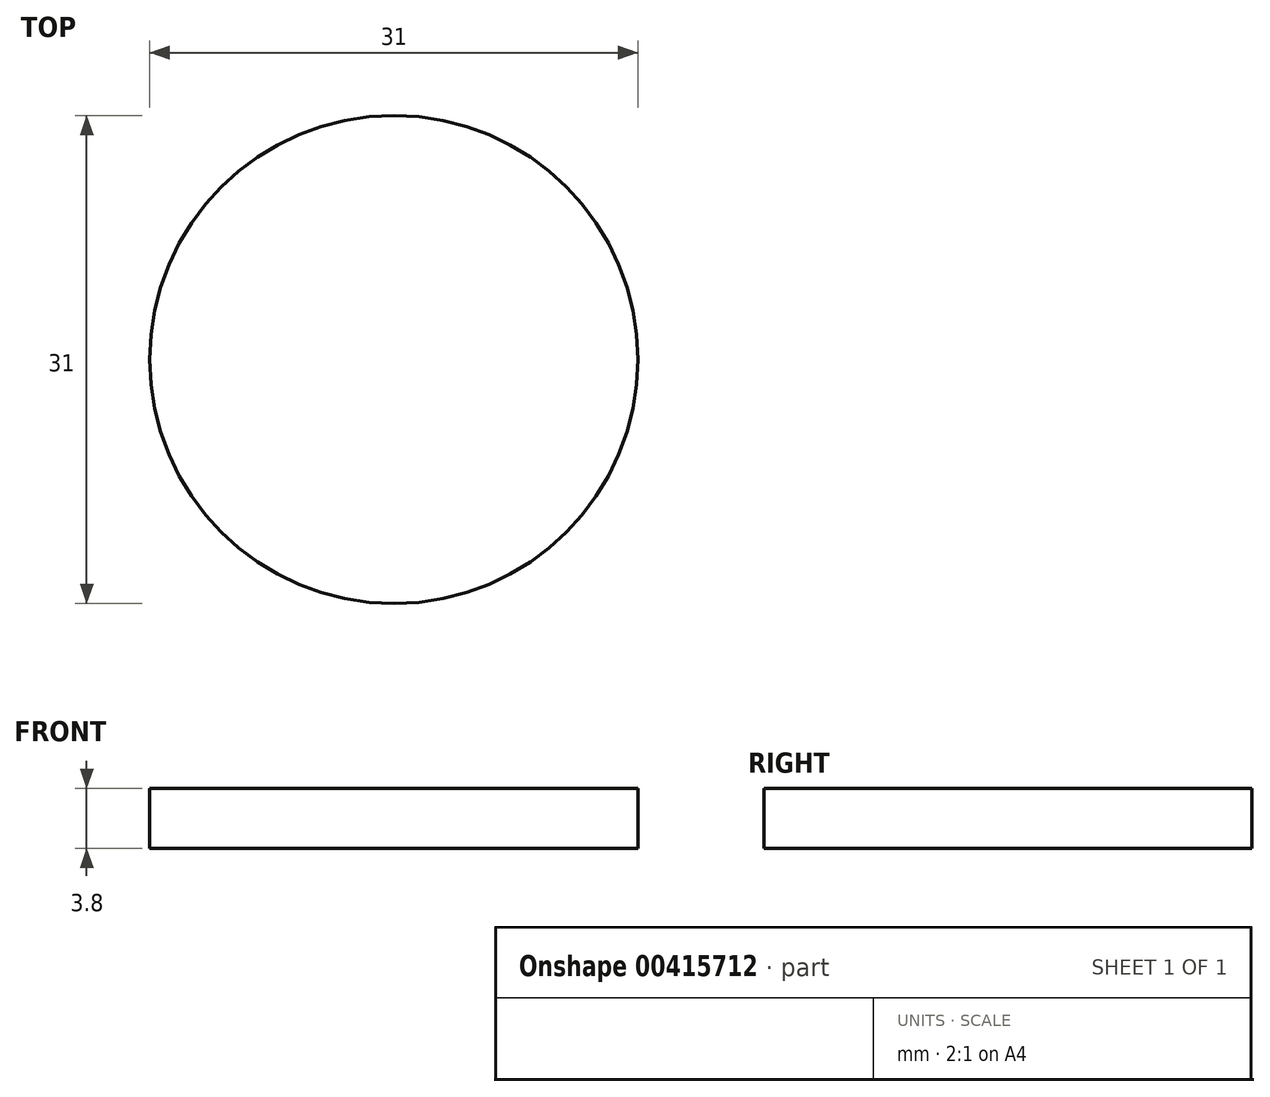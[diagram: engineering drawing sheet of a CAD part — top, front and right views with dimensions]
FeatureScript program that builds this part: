
annotation { "Feature Type Name" : "Feature", "Feature Type Description" : "" }
export const myFeature = defineFeature(function(context is Context, id is Id, definition is map)
    precondition{}
    {
        {
            var Q0;
            Q0=qCreatedBy(makeId("Top.planeOp"),FACE);
            var sketch = newSketch(context, id + "F0", { "sketchPlane" : qUnion([Q0])});
            skCircle(sketch, "E0", {"center": v(0, 0) * mm, "radius": 15.5 * mm});
            skSolve(sketch);
        }
        {
            var Q0;
            Q0 = qSketchRegion(id + "F0", true);
            extrude(context, id + "F1", {"entities" : qUnion([Q0]), "depth" : 3.8 * mm});
        }
    });
